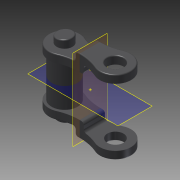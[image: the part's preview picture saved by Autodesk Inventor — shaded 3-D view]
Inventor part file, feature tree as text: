
AUTODESK INVENTOR PART (.ipt)
format: ipt  version: 2015 SP1 (Build 190203100, 203)  size: 528,896 bytes
history: native  units: in
note: dims shown in document units (in); Inventor stores cm internally (conversion verified against a paired STEP export)
features: other x3, imported_body x1, plane x1
ambient origin geometry x8: Origin, YZ Plane, XZ Plane, XY Plane, X Axis, Y Axis, Z Axis, Center Point
bodies: Solid1 (feature_tree)
feature tree (5):
  other  "Chain HS Link"
  other  "Work Point2"
  imported_body  "Base1"
  other  "mid-plane"
  plane  "Work Plane2"
